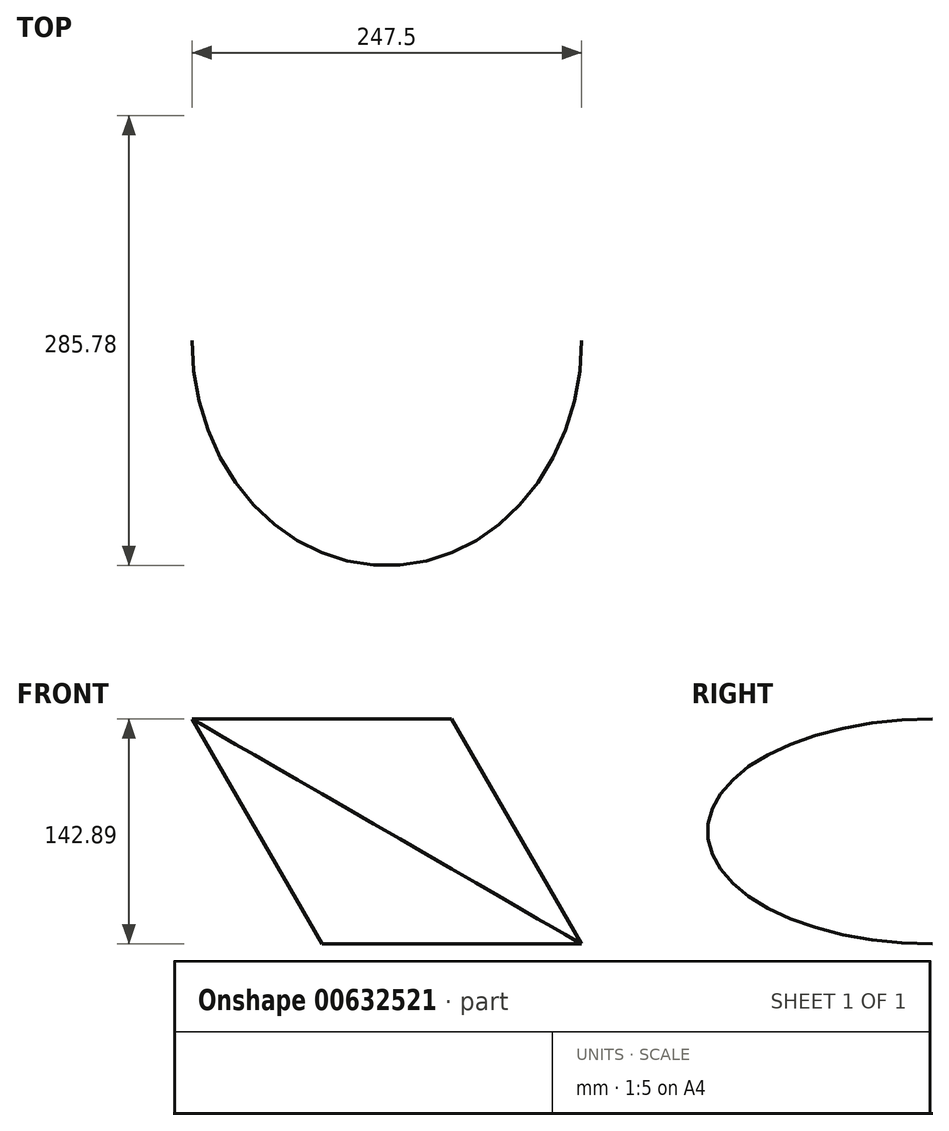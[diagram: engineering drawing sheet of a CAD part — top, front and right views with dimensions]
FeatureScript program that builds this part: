
annotation { "Feature Type Name" : "Feature", "Feature Type Description" : "" }
export const myFeature = defineFeature(function(context is Context, id is Id, definition is map)
    precondition{}
    {
        {
            var Q0;
            Q0=qCreatedBy(makeId("Front.planeOp"),FACE);
            var sketch = newSketch(context, id + "F0", { "sketchPlane" : qUnion([Q0])});
            skCircle(sketch, "E0.cCircle", {"center": v(0, 0) * mm, "radius": 47.63 * mm, "construction": true});
            skLineSegment(sketch, "E0.0", {"start": v(82.5, -47.63) * mm, "end": v(-82.5, -47.63) * mm});
            skLineSegment(sketch, "E0.1", {"start": v(-82.5, -47.63) * mm, "end": v(0, 95.26) * mm});
            skLineSegment(sketch, "E0.2", {"start": v(0, 95.26) * mm, "end": v(82.5, -47.63) * mm});
            skPoint(sketch, "E0.0.midPoint", {"position": v(0, -47.63) * mm});
            skSolve(sketch);
        }
        {
            var Q0;
            Q0=makeQuery(id+"F0.imprint","IMPRINT",FACE,{"disambiguationData":[TD([[makeQuery(id+"F0.imprint","IMPRINT",EDGE,{"derivedFrom":sQuery(id+"F0.wireOp",EDGE,"E0.0")}),-1.0]])]});
            var Q1;
            Q1=sQuery(id+"F0.wireOp",EDGE,"E0.1");
            revolve(context, id + "F1", {"entities" : qUnion([Q0]), "axis" : qUnion([Q1]), "revolveType" : RevolveType.FULL});
        }
    });
